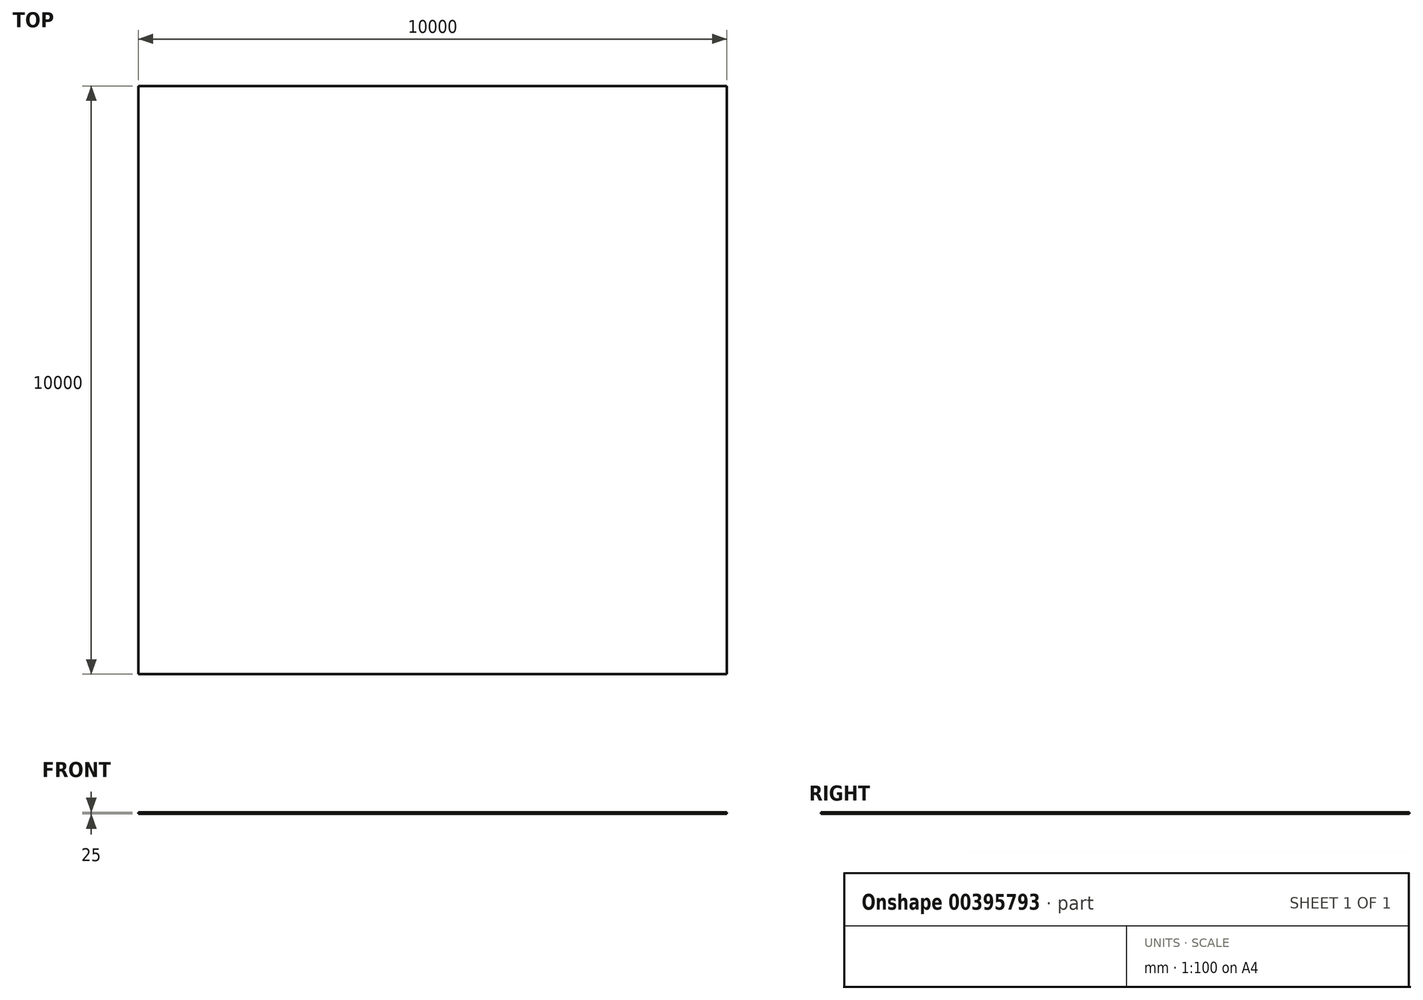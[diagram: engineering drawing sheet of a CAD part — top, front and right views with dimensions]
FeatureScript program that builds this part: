
annotation { "Feature Type Name" : "Feature", "Feature Type Description" : "" }
export const myFeature = defineFeature(function(context is Context, id is Id, definition is map)
    precondition{}
    {
        {
            var Q0;
            Q0=qCreatedBy(makeId("Top.planeOp"),FACE);
            var sketch = newSketch(context, id + "F0", { "sketchPlane" : qUnion([Q0])});
            skLineSegment(sketch, "E0.bottom", {"start": v(0, 0) * mm, "end": v(10000, 0) * mm});
            skLineSegment(sketch, "E0.top", {"start": v(0, 10000) * mm, "end": v(10000, 10000) * mm});
            skLineSegment(sketch, "E0.left", {"start": v(0, 0) * mm, "end": v(0, 10000) * mm});
            skLineSegment(sketch, "E0.right", {"start": v(10000, 0) * mm, "end": v(10000, 10000) * mm});
            skSolve(sketch);
        }
        {
            var Q0;
            Q0=makeQuery(id+"F0.imprint","IMPRINT",FACE,{"disambiguationData":[TD([[makeQuery(id+"F0.imprint","IMPRINT",EDGE,{"derivedFrom":sQuery(id+"F0.wireOp",EDGE,"E0.bottom")}),1.0]])]});
            extrude(context, id + "F1", {"entities" : qUnion([Q0]), "depth" : 25 * mm, "offsetDistance" : 25 * mm});
        }
    });
